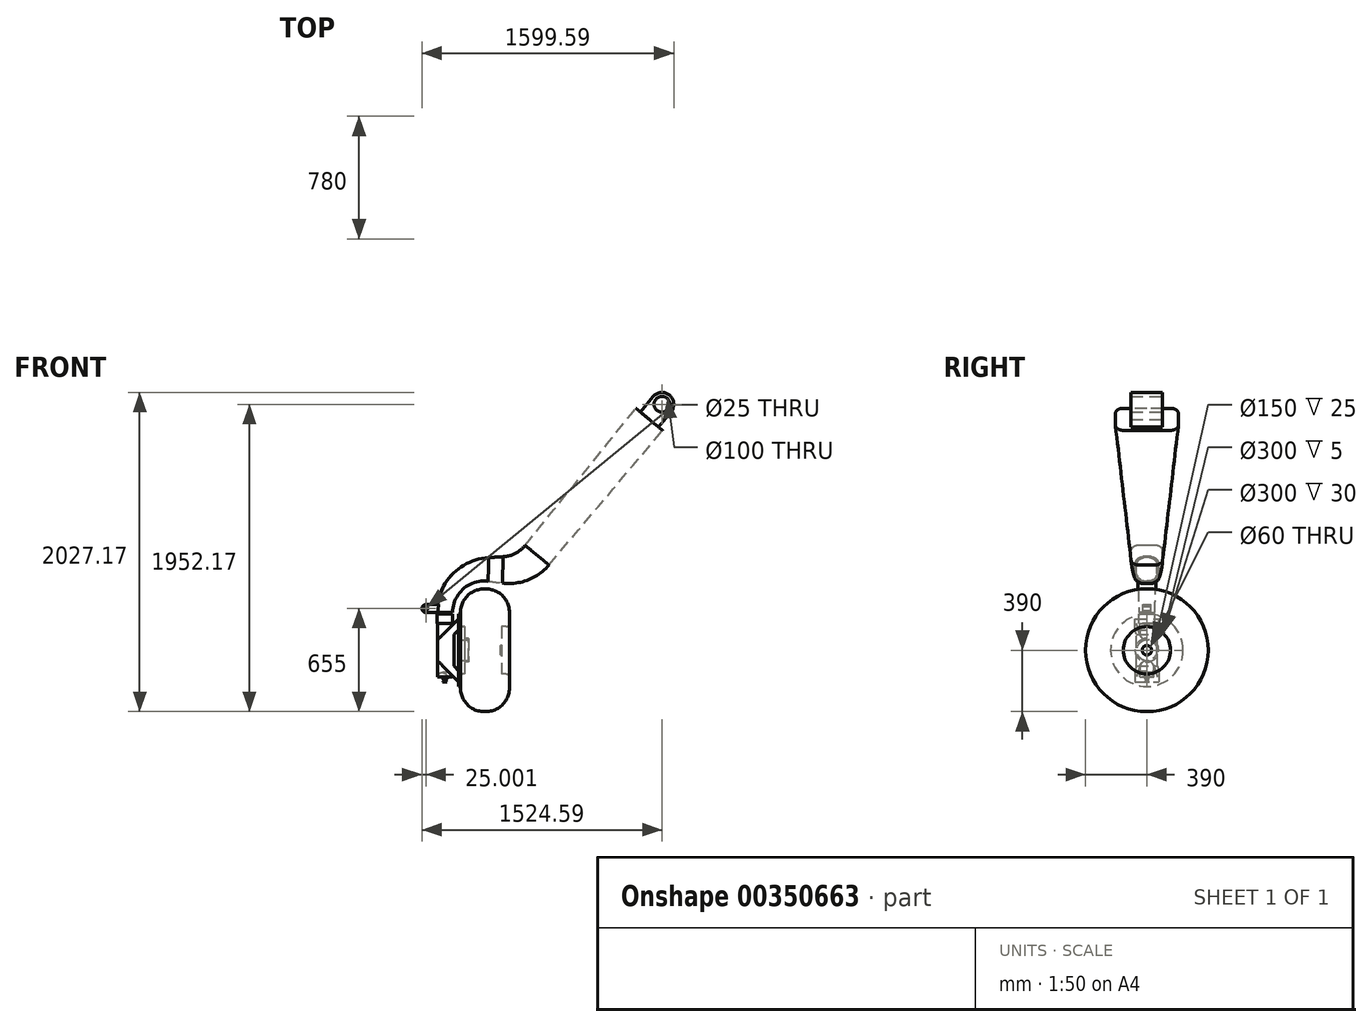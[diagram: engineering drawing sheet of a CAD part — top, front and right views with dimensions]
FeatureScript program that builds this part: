
annotation { "Feature Type Name" : "Feature", "Feature Type Description" : "" }
export const myFeature = defineFeature(function(context is Context, id is Id, definition is map)
    precondition{}
    {
        {
            var Q0;
            Q0=qCreatedBy(makeId("Front.planeOp"),FACE);
            var sketch = newSketch(context, id + "F0", { "sketchPlane" : qUnion([Q0])});
            skLineSegment(sketch, "E0.top", {"start": v(-5, 390) * mm, "end": v(5, 390) * mm});
            skLineSegment(sketch, "E0.left", {"start": v(-155, 170) * mm, "end": v(-155, 240) * mm});
            skLineSegment(sketch, "E0.right", {"start": v(155, 170) * mm, "end": v(155, 240) * mm});
            skPoint(sketch, "E1.visualSharp", {"position": v(-155, 390) * mm});
            skArc(sketch, "E1.filletArc", {"start": v(-5, 390) * mm, "mid": v(-111.07, 346.07) * mm, "end": v(-155, 240) * mm});
            skPoint(sketch, "E2.visualSharp", {"position": v(155, 390) * mm});
            skArc(sketch, "E2.filletArc", {"start": v(155, 240) * mm, "mid": v(111.07, 346.07) * mm, "end": v(5, 390) * mm});
            skLineSegment(sketch, "E3", {"start": v(-130, 75) * mm, "end": v(-105, 75) * mm});
            skLineSegment(sketch, "E4", {"start": v(-105, 75) * mm, "end": v(-105, 30) * mm});
            skLineSegment(sketch, "E5", {"start": v(-105, 30) * mm, "end": v(105, 30) * mm});
            skLineSegment(sketch, "E6", {"start": v(105, 30) * mm, "end": v(105, 150) * mm});
            skLineSegment(sketch, "E7", {"start": v(105, 150) * mm, "end": v(135, 150) * mm});
            skPoint(sketch, "E8.orphan", {"position": v(-155, 0) * mm});
            skPoint(sketch, "E9.visualSharp", {"position": v(155, 150) * mm});
            skArc(sketch, "E9.filletArc", {"start": v(135, 150) * mm, "mid": v(149.14, 155.86) * mm, "end": v(155, 170) * mm});
            skLineSegment(sketch, "E10", {"start": v(-280.75, 0) * mm, "end": v(393.95, 0) * mm});
            skLineSegment(sketch, "E11", {"start": v(-135, 150) * mm, "end": v(-130, 150) * mm});
            skLineSegment(sketch, "E12", {"start": v(-130, 150) * mm, "end": v(-130, 75) * mm});
            skPoint(sketch, "E13.visualSharp", {"position": v(-155, 150) * mm});
            skArc(sketch, "E13.filletArc", {"start": v(-155, 170) * mm, "mid": v(-149.14, 155.86) * mm, "end": v(-135, 150) * mm});
            skSolve(sketch);
        }
        {
            var Q0;
            Q0=qCreatedBy(makeId("Front.planeOp"),FACE);
            var sketch = newSketch(context, id + "F1", { "sketchPlane" : qUnion([Q0])});
            skLineSegment(sketch, "E14", {"start": v(-167, 230.07) * mm, "end": v(-157, 230.07) * mm});
            skLineSegment(sketch, "E15", {"start": v(-157, 230.07) * mm, "end": v(-157, 65) * mm});
            skLineSegment(sketch, "E16", {"start": v(-157, 65) * mm, "end": v(-105, 65) * mm});
            skLineSegment(sketch, "E17", {"start": v(-105, 65) * mm, "end": v(-105, 30) * mm});
            skLineSegment(sketch, "E18", {"start": v(-105, 30) * mm, "end": v(100, 30) * mm});
            skLineSegment(sketch, "E19", {"start": v(105, 25) * mm, "end": v(105, 0) * mm});
            skLineSegment(sketch, "E20", {"start": v(105, 0) * mm, "end": v(-167, 0) * mm});
            skLineSegment(sketch, "E21", {"start": v(-167, 0) * mm, "end": v(-167, 230.07) * mm});
            skPoint(sketch, "E22.visualSharp", {"position": v(105, 30) * mm});
            skArc(sketch, "E22.filletArc", {"start": v(105, 25) * mm, "mid": v(103.54, 28.54) * mm, "end": v(100, 30) * mm});
            skSolve(sketch);
        }
        {
            var Q0;
            Q0=qCreatedBy(makeId("Front.planeOp"),FACE);
            var sketch = newSketch(context, id + "F2", { "sketchPlane" : qUnion([Q0])});
            skLineSegment(sketch, "E23", {"start": v(-205, 0) * mm, "end": v(-205, 240) * mm});
            skLineSegment(sketch, "E24", {"start": v(-305, 0) * mm, "end": v(-305, 240) * mm});
            skArc(sketch, "E25", {"start": v(20.62, 438.35) * mm, "mid": v(-137.05, 390.2) * mm, "end": v(-205, 240) * mm});
            skLineSegment(sketch, "E26", {"start": v(-205, 240) * mm, "end": v(-305, 240) * mm, "construction": true});
            skLineSegment(sketch, "E27", {"start": v(20.62, 438.35) * mm, "end": v(22.33, 588.34) * mm, "construction": true});
            skArc(sketch, "E28", {"start": v(22.33, 588.34) * mm, "mid": v(-210.33, 479) * mm, "end": v(-305, 240) * mm});
            skLineSegment(sketch, "E29", {"start": v(22.33, 588.34) * mm, "end": v(89.49, 592.52) * mm});
            skArc(sketch, "E30", {"start": v(401.06, 544.79) * mm, "mid": v(264.57, 448.23) * mm, "end": v(98.57, 428.28) * mm});
            skArc(sketch, "E31", {"start": v(89.49, 592.52) * mm, "mid": v(177.07, 616.48) * mm, "end": v(247.85, 673.34) * mm});
            skLineSegment(sketch, "E32", {"start": v(247.85, 673.34) * mm, "end": v(401.06, 544.79) * mm, "construction": true});
            skLineSegment(sketch, "E33", {"start": v(324.45, 609.07) * mm, "end": v(1043.85, 1466.41) * mm});
            skLineSegment(sketch, "E34", {"start": v(401.06, 544.79) * mm, "end": v(1128.12, 1395.7) * mm});
            skLineSegment(sketch, "E35", {"start": v(247.85, 673.34) * mm, "end": v(959.59, 1537.12) * mm});
            skLineSegment(sketch, "E36", {"start": v(959.59, 1537.12) * mm, "end": v(1128.12, 1395.7) * mm, "construction": true});
            skArc(sketch, "E37", {"start": v(21.47, 513.35) * mm, "mid": v(-173.83, 434.4) * mm, "end": v(-255, 240) * mm});
            skLineSegment(sketch, "E38", {"start": v(21.47, 513.35) * mm, "end": v(113.82, 512.3) * mm});
            skArc(sketch, "E39", {"start": v(113.82, 512.3) * mm, "mid": v(230, 537.02) * mm, "end": v(324.45, 609.07) * mm});
            skLineSegment(sketch, "E40", {"start": v(20.62, 438.35) * mm, "end": v(98.57, 428.28) * mm});
            skSolve(sketch);
        }
        {
            var Q0;
            Q0=qCreatedBy(makeId("Front.planeOp"),FACE);
            var sketch = newSketch(context, id + "F3", { "sketchPlane" : qUnion([Q0])});
            skLineSegment(sketch, "E41.0", {"start": v(-205, 0) * mm, "end": v(-205, 240) * mm, "construction": true});
            skLineSegment(sketch, "E42.0", {"start": v(-305, 0) * mm, "end": v(-305, 240) * mm, "construction": true});
            skLineSegment(sketch, "E43", {"start": v(-305, 240) * mm, "end": v(-205, 240) * mm, "construction": true});
            skLineSegment(sketch, "E44", {"start": v(-255, 230) * mm, "end": v(-255, 0) * mm, "construction": true});
            skPoint(sketch, "E44.startSnap0", {"position": v(-255, 240) * mm});
            skLineSegment(sketch, "E45", {"start": v(-210, 0) * mm, "end": v(-210, 170) * mm});
            skLineSegment(sketch, "E46", {"start": v(-210, 170) * mm, "end": v(-205, 170) * mm});
            skLineSegment(sketch, "E47", {"start": v(-255, 230) * mm, "end": v(-205, 230) * mm, "construction": true});
            skLineSegment(sketch, "E48", {"start": v(-205, 230) * mm, "end": v(-205, 170) * mm});
            skLineSegment(sketch, "E49", {"start": v(-225, 230) * mm, "end": v(-225, 0.12) * mm});
            skPoint(sketch, "E49.endSnap0", {"position": v(-217.5, 0.12) * mm});
            skLineSegment(sketch, "E50", {"start": v(-225, 230) * mm, "end": v(-205, 230) * mm});
            skLineSegment(sketch, "E51", {"start": v(-210, 0) * mm, "end": v(-210, -170) * mm});
            skLineSegment(sketch, "E52", {"start": v(-225, -200) * mm, "end": v(-240, -200) * mm});
            skLineSegment(sketch, "E53", {"start": v(-225, -100) * mm, "end": v(-225, 0.12) * mm});
            skLineSegment(sketch, "E54", {"start": v(-225, -200) * mm, "end": v(-255, -200) * mm});
            skLineSegment(sketch, "E55", {"start": v(-255, -200) * mm, "end": v(-255, -100) * mm});
            skLineSegment(sketch, "E56", {"start": v(-255, -100) * mm, "end": v(-225, -100) * mm});
            skPoint(sketch, "E57.visualSharp", {"position": v(-210, -200) * mm});
            skArc(sketch, "E57.filletArc", {"start": v(-240, -200) * mm, "mid": v(-218.79, -191.21) * mm, "end": v(-210, -170) * mm});
            skSolve(sketch);
        }
        {
            var Q0;
            Q0=qCreatedBy(makeId("Front.planeOp"),FACE);
            var sketch = newSketch(context, id + "F4", { "sketchPlane" : qUnion([Q0])});
            skPoint(sketch, "E58.0", {"position": v(-167, 115.04) * mm});
            skLineSegment(sketch, "E59.0", {"start": v(-167, 115.04) * mm, "end": v(-167, 200) * mm});
            skPoint(sketch, "E60.orphan", {"position": v(-255, 230) * mm});
            skPoint(sketch, "E61.orphan", {"position": v(-167, 230.07) * mm});
            skLineSegment(sketch, "E62", {"start": v(-167, 200) * mm, "end": v(-367, 0) * mm});
            skLineSegment(sketch, "E63", {"start": v(-367, 0) * mm, "end": v(-197, 0) * mm});
            skLineSegment(sketch, "E64", {"start": v(-167, 130) * mm, "end": v(-197, 100) * mm});
            skLineSegment(sketch, "E65", {"start": v(-197, 100) * mm, "end": v(-197, 0) * mm});
            skPoint(sketch, "E66.orphan", {"position": v(-167, 0) * mm});
            skSolve(sketch);
        }
        {
            var Q0;
            Q0=qCreatedBy(makeId("Top.planeOp"),FACE);
            var sketch = newSketch(context, id + "F5", { "sketchPlane" : qUnion([Q0])});
            skPoint(sketch, "E67.0", {"position": v(-210, 0) * mm});
            skPoint(sketch, "E68.0", {"position": v(-255, 0) * mm});
            skLineSegment(sketch, "E69", {"start": v(-167, -75) * mm, "end": v(-367, -75) * mm});
            skLineSegment(sketch, "E70", {"start": v(-367, -75) * mm, "end": v(-367, 75) * mm});
            skLineSegment(sketch, "E71", {"start": v(-367, 75) * mm, "end": v(-167, 75) * mm});
            skLineSegment(sketch, "E72", {"start": v(-167, -75) * mm, "end": v(-167, 75) * mm, "construction": true});
            skCircle(sketch, "E73", {"center": v(-255, 0) * mm, "radius": 45 * mm, "construction": true});
            skArc(sketch, "E74.0", {"start": v(-268.31, 45.07) * mm, "mid": v(-302, 0) * mm, "end": v(-268.31, -45.07) * mm});
            skLineSegment(sketch, "E75", {"start": v(-268.31, -45.07) * mm, "end": v(-167, -75) * mm});
            skLineSegment(sketch, "E76", {"start": v(-268.31, 45.07) * mm, "end": v(-167, 75) * mm});
            skSolve(sketch);
        }
        {
            var Q0;
            Q0=sQuery(id+"F2.wireOp",EDGE,"E37");
            var Q1;
            Q1=sQuery(id+"F3.wireOp",VERTEX,"E44.startSnap0");
            cPlane(context, id + "F6", {"entities" : qUnion([Q0, Q1]), "cplaneType" : CPlaneType.CURVE_POINT, "offset" : 25 * mm, "width" : 150 * mm, "height" : 150 * mm});
        }
        {
            var Q0;
            Q0=sQuery(id+"F2.wireOp",EDGE,"E37");
            var Q1;
            Q1=sQuery(id+"F2.wireOp",VERTEX,"E37.start");
            cPlane(context, id + "F7", {"entities" : qUnion([Q0, Q1]), "cplaneType" : CPlaneType.CURVE_POINT, "offset" : 25 * mm, "width" : 150 * mm, "height" : 150 * mm});
        }
        {
            var Q0;
            Q0=qCreatedBy(id+"F6.planeOp",FACE);
            var sketch = newSketch(context, id + "F8", { "sketchPlane" : qUnion([Q0])});
            skPoint(sketch, "E77.0", {"position": v(-205, 0) * mm});
            skPoint(sketch, "E78.0", {"position": v(-255, 0) * mm});
            skCircle(sketch, "E79", {"center": v(-255, 0) * mm, "radius": 50 * mm});
            skSolve(sketch);
        }
        {
            var Q0;
            Q0=qCreatedBy(makeId("Front.planeOp"),FACE);
            var sketch = newSketch(context, id + "F9", { "sketchPlane" : qUnion([Q0])});
            skPoint(sketch, "E80.0", {"position": v(-205, 240) * mm});
            skPoint(sketch, "E81.0", {"position": v(20.62, 438.35) * mm});
            skArc(sketch, "E82", {"start": v(20.62, 438.35) * mm, "mid": v(-137.05, 390.2) * mm, "end": v(-205, 240) * mm});
            skPoint(sketch, "E83.0", {"position": v(-305, 240) * mm});
            skPoint(sketch, "E84.0", {"position": v(22.33, 588.34) * mm});
            skArc(sketch, "E85", {"start": v(22.33, 588.34) * mm, "mid": v(-210.33, 479) * mm, "end": v(-305, 240) * mm});
            skSolve(sketch);
        }
        {
            var Q0;
            Q0=qCreatedBy(id+"F7.planeOp",FACE);
            var sketch = newSketch(context, id + "F10", { "sketchPlane" : qUnion([Q0])});
            skPoint(sketch, "E86.0", {"position": v(0, 513.56) * mm});
            skLineSegment(sketch, "E87.bottom", {"start": v(-15, 438.56) * mm, "end": v(15, 438.56) * mm});
            skLineSegment(sketch, "E87.top", {"start": v(-15, 588.56) * mm, "end": v(15, 588.56) * mm});
            skLineSegment(sketch, "E87.left", {"start": v(-65, 488.56) * mm, "end": v(-65, 538.56) * mm});
            skLineSegment(sketch, "E87.right", {"start": v(65, 488.56) * mm, "end": v(65, 538.56) * mm});
            skPoint(sketch, "E88.0", {"position": v(0, 438.56) * mm});
            skPoint(sketch, "E89.visualSharp", {"position": v(65, 588.56) * mm});
            skArc(sketch, "E89.filletArc", {"start": v(65, 538.56) * mm, "mid": v(50.36, 573.91) * mm, "end": v(15, 588.56) * mm});
            skPoint(sketch, "E90.visualSharp", {"position": v(-65, 588.56) * mm});
            skArc(sketch, "E90.filletArc", {"start": v(-15, 588.56) * mm, "mid": v(-50.36, 573.91) * mm, "end": v(-65, 538.56) * mm});
            skPoint(sketch, "E91.visualSharp", {"position": v(-65, 438.56) * mm});
            skArc(sketch, "E91.filletArc", {"start": v(-65, 488.56) * mm, "mid": v(-50.36, 453.2) * mm, "end": v(-15, 438.56) * mm});
            skPoint(sketch, "E92.visualSharp", {"position": v(65, 438.56) * mm});
            skArc(sketch, "E92.filletArc", {"start": v(15, 438.56) * mm, "mid": v(50.36, 453.2) * mm, "end": v(65, 488.56) * mm});
            skSolve(sketch);
        }
        {
            var Q0;
            Q0=qCreatedBy(makeId("Front.planeOp"),FACE);
            var sketch = newSketch(context, id + "F11", { "sketchPlane" : qUnion([Q0])});
            skPoint(sketch, "E93.0", {"position": v(20.62, 438.35) * mm});
            skPoint(sketch, "E94.0", {"position": v(22.33, 588.34) * mm});
            skLineSegment(sketch, "E95", {"start": v(20.62, 438.35) * mm, "end": v(111.11, 426.66) * mm});
            skLineSegment(sketch, "E96", {"start": v(22.33, 588.34) * mm, "end": v(116.4, 594.2) * mm});
            skLineSegment(sketch, "E97", {"start": v(116.4, 594.2) * mm, "end": v(111.11, 426.66) * mm});
            skLineSegment(sketch, "E98", {"start": v(113.76, 510.43) * mm, "end": v(21.47, 513.35) * mm, "construction": true});
            skSolve(sketch);
        }
        {
            var Q0;
            Q0=sQuery(id+"F11.wireOp",EDGE,"E98");
            var Q1;
            Q1=sQuery(id+"F11.wireOp",VERTEX,"E98.start");
            cPlane(context, id + "F12", {"entities" : qUnion([Q0, Q1]), "cplaneType" : CPlaneType.CURVE_POINT, "offset" : 25 * mm, "width" : 150 * mm, "height" : 150 * mm});
        }
        {
            var Q0;
            Q0=qCreatedBy(id+"F12.planeOp",FACE);
            var sketch = newSketch(context, id + "F13", { "sketchPlane" : qUnion([Q0])});
            skPoint(sketch, "E99.0", {"position": v(0, 513.77) * mm});
            skLineSegment(sketch, "E100.bottom", {"start": v(-25, 429.96) * mm, "end": v(25, 429.96) * mm});
            skLineSegment(sketch, "E100.top", {"start": v(-25, 597.58) * mm, "end": v(25, 597.58) * mm});
            skLineSegment(sketch, "E100.left", {"start": v(-75, 479.96) * mm, "end": v(-75, 547.58) * mm});
            skLineSegment(sketch, "E100.right", {"start": v(75, 479.96) * mm, "end": v(75, 547.58) * mm});
            skPoint(sketch, "E101.0", {"position": v(0, 597.58) * mm});
            skPoint(sketch, "E102.0", {"position": v(0, 429.96) * mm});
            skPoint(sketch, "E103.visualSharp", {"position": v(75, 429.96) * mm});
            skArc(sketch, "E103.filletArc", {"start": v(25, 429.96) * mm, "mid": v(60.36, 444.6) * mm, "end": v(75, 479.96) * mm});
            skPoint(sketch, "E104.visualSharp", {"position": v(75, 597.58) * mm});
            skArc(sketch, "E104.filletArc", {"start": v(75, 547.58) * mm, "mid": v(60.36, 582.93) * mm, "end": v(25, 597.58) * mm});
            skPoint(sketch, "E105.visualSharp", {"position": v(-75, 597.58) * mm});
            skArc(sketch, "E105.filletArc", {"start": v(-25, 597.58) * mm, "mid": v(-60.36, 582.93) * mm, "end": v(-75, 547.58) * mm});
            skPoint(sketch, "E106.visualSharp", {"position": v(-75, 429.96) * mm});
            skArc(sketch, "E106.filletArc", {"start": v(-75, 479.96) * mm, "mid": v(-60.36, 444.6) * mm, "end": v(-25, 429.96) * mm});
            skSolve(sketch);
        }
        {
            var Q0;
            Q0=qCreatedBy(makeId("Front.planeOp"),FACE);
            var sketch = newSketch(context, id + "F14", { "sketchPlane" : qUnion([Q0])});
            skPoint(sketch, "E107.0", {"position": v(111.11, 426.66) * mm});
            skPoint(sketch, "E108.0", {"position": v(116.4, 594.2) * mm});
            skArc(sketch, "E109", {"start": v(111.11, 426.66) * mm, "mid": v(273.33, 446.39) * mm, "end": v(406.34, 541.32) * mm});
            skArc(sketch, "E110", {"start": v(116.4, 594.2) * mm, "mid": v(193.48, 615.48) * mm, "end": v(255.46, 666) * mm});
            skLineSegment(sketch, "E111", {"start": v(406.34, 541.32) * mm, "end": v(255.46, 666) * mm});
            skLineSegment(sketch, "E112", {"start": v(330.9, 603.66) * mm, "end": v(1043.85, 1466.41) * mm, "construction": true});
            skLineSegment(sketch, "E113", {"start": v(406.34, 541.32) * mm, "end": v(1128.12, 1395.7) * mm, "construction": true});
            skLineSegment(sketch, "E114", {"start": v(255.46, 666) * mm, "end": v(959.59, 1537.12) * mm, "construction": true});
            skPoint(sketch, "E115.0", {"position": v(113.76, 510.43) * mm});
            skArc(sketch, "E116", {"start": v(113.76, 510.43) * mm, "mid": v(233.6, 530.78) * mm, "end": v(330.9, 603.66) * mm, "construction": true});
            skSolve(sketch);
        }
        {
            var Q0;
            Q0=sQuery(id+"F14.wireOp",EDGE,"E111");
            cPoint(context, id + "F15", {"entities" : qUnion([Q0]), "parameter" : 0.5});
        }
        {
            var Q0;
            Q0=sQuery(id+"F14.wireOp",EDGE,"E116");
            var Q1;
            Q1=qCreatedBy(id+"F15",VERTEX);
            cPlane(context, id + "F16", {"entities" : qUnion([Q0, Q1]), "cplaneType" : CPlaneType.CURVE_POINT, "offset" : 25 * mm, "width" : 150 * mm, "height" : 150 * mm});
        }
        {
            var Q0;
            Q0=qCreatedBy(id+"F16.planeOp",FACE);
            var sketch = newSketch(context, id + "F17", { "sketchPlane" : qUnion([Q0])});
            skPoint(sketch, "E117.0", {"position": v(-129.46, 0) * mm});
            skPoint(sketch, "E118.0", {"position": v(-31.6, 0) * mm});
            skLineSegment(sketch, "E119.bottom", {"start": v(-81.6, 100) * mm, "end": v(-177.32, 100) * mm});
            skLineSegment(sketch, "E119.top", {"start": v(-81.6, -100) * mm, "end": v(-177.32, -100) * mm});
            skLineSegment(sketch, "E119.left", {"start": v(-31.6, 50) * mm, "end": v(-31.6, -50) * mm});
            skLineSegment(sketch, "E119.right", {"start": v(-227.32, 50) * mm, "end": v(-227.32, -50) * mm});
            skPoint(sketch, "E120.visualSharp", {"position": v(-31.6, -100) * mm});
            skArc(sketch, "E120.filletArc", {"start": v(-81.6, -100) * mm, "mid": v(-46.25, -85.36) * mm, "end": v(-31.6, -50) * mm});
            skPoint(sketch, "E121.visualSharp", {"position": v(-227.32, -100) * mm});
            skArc(sketch, "E121.filletArc", {"start": v(-227.32, -50) * mm, "mid": v(-212.68, -85.36) * mm, "end": v(-177.32, -100) * mm});
            skPoint(sketch, "E122.visualSharp", {"position": v(-227.32, 100) * mm});
            skArc(sketch, "E122.filletArc", {"start": v(-177.32, 100) * mm, "mid": v(-212.68, 85.36) * mm, "end": v(-227.32, 50) * mm});
            skPoint(sketch, "E123.visualSharp", {"position": v(-31.6, 100) * mm});
            skArc(sketch, "E123.filletArc", {"start": v(-31.6, 50) * mm, "mid": v(-46.25, 85.36) * mm, "end": v(-81.6, 100) * mm});
            skSolve(sketch);
        }
        {
            var Q0;
            Q0=sQuery(id+"F14.wireOp",EDGE,"E112");
            var Q1;
            Q1=sQuery(id+"F14.wireOp",VERTEX,"E112.end");
            cPlane(context, id + "F18", {"entities" : qUnion([Q0, Q1]), "cplaneType" : CPlaneType.CURVE_POINT, "offset" : 25 * mm, "width" : 150 * mm, "height" : 150 * mm});
        }
        {
            var Q0;
            Q0=qCreatedBy(id+"F18.planeOp",FACE);
            var sketch = newSketch(context, id + "F19", { "sketchPlane" : qUnion([Q0])});
            skPoint(sketch, "E124.0", {"position": v(-129.46, 0) * mm});
            skPoint(sketch, "E125.0", {"position": v(-19.47, 0) * mm});
            skLineSegment(sketch, "E126.bottom", {"start": v(-69.47, 200) * mm, "end": v(-189.46, 200) * mm});
            skLineSegment(sketch, "E126.top", {"start": v(-69.47, -200) * mm, "end": v(-189.46, -200) * mm});
            skLineSegment(sketch, "E126.left", {"start": v(-19.47, 150) * mm, "end": v(-19.47, -150) * mm});
            skLineSegment(sketch, "E126.right", {"start": v(-239.46, 150) * mm, "end": v(-239.46, -150) * mm});
            skPoint(sketch, "E127.visualSharp", {"position": v(-239.46, -200) * mm});
            skArc(sketch, "E127.filletArc", {"start": v(-239.46, -150) * mm, "mid": v(-224.81, -185.36) * mm, "end": v(-189.46, -200) * mm});
            skPoint(sketch, "E128.visualSharp", {"position": v(-239.46, 200) * mm});
            skArc(sketch, "E128.filletArc", {"start": v(-189.46, 200) * mm, "mid": v(-224.81, 185.36) * mm, "end": v(-239.46, 150) * mm});
            skPoint(sketch, "E129.visualSharp", {"position": v(-19.47, 200) * mm});
            skArc(sketch, "E129.filletArc", {"start": v(-19.47, 150) * mm, "mid": v(-34.11, 185.36) * mm, "end": v(-69.47, 200) * mm});
            skPoint(sketch, "E130.visualSharp", {"position": v(-19.47, -200) * mm});
            skArc(sketch, "E130.filletArc", {"start": v(-69.47, -200) * mm, "mid": v(-34.11, -185.36) * mm, "end": v(-19.47, -150) * mm});
            skSolve(sketch);
        }
        {
            var Q0;
            Q0=qCreatedBy(makeId("Front.planeOp"),FACE);
            var sketch = newSketch(context, id + "F20", { "sketchPlane" : qUnion([Q0])});
            skPoint(sketch, "E131.0", {"position": v(406.34, 541.32) * mm});
            skPoint(sketch, "E132.0", {"position": v(1128.65, 1396.34) * mm});
            skPoint(sketch, "E133.0", {"position": v(255.46, 666) * mm});
            skPoint(sketch, "E134.0", {"position": v(959.06, 1536.48) * mm});
            skLineSegment(sketch, "E135", {"start": v(406.34, 541.32) * mm, "end": v(1128.65, 1396.34) * mm});
            skLineSegment(sketch, "E136", {"start": v(255.46, 666) * mm, "end": v(959.06, 1536.48) * mm});
            skSolve(sketch);
        }
        {
            var Q0;
            Q0=qCreatedBy(makeId("Front.planeOp"),FACE);
            var sketch = newSketch(context, id + "F21", { "sketchPlane" : qUnion([Q0])});
            skPoint(sketch, "E137.0", {"position": v(-255, 240) * mm});
            skPoint(sketch, "E138.0", {"position": v(-225, -100) * mm});
            skLineSegment(sketch, "E139.bottom", {"start": v(-255, 240) * mm, "end": v(-225, 240) * mm});
            skLineSegment(sketch, "E139.top", {"start": v(-255, -100) * mm, "end": v(-225, -100) * mm});
            skLineSegment(sketch, "E139.left", {"start": v(-255, 240) * mm, "end": v(-255, -100) * mm});
            skLineSegment(sketch, "E139.right", {"start": v(-225, 240) * mm, "end": v(-225, -100) * mm});
            skSolve(sketch);
        }
        {
            var Q0;
            Q0=qCreatedBy(makeId("Front.planeOp"),FACE);
            var sketch = newSketch(context, id + "F22", { "sketchPlane" : qUnion([Q0])});
            skPoint(sketch, "E140.0", {"position": v(-255, 240) * mm});
            skArc(sketch, "E141", {"start": v(-250.39, 290) * mm, "mid": v(-253.84, 265.1) * mm, "end": v(-255, 240) * mm});
            skLineSegment(sketch, "E142", {"start": v(-255, 240) * mm, "end": v(-375.39, 240) * mm});
            skLineSegment(sketch, "E143", {"start": v(-400.39, 265) * mm, "end": v(-400.39, 265) * mm});
            skLineSegment(sketch, "E144", {"start": v(-375.39, 290) * mm, "end": v(-250.39, 290) * mm});
            skPoint(sketch, "E145.visualSharp", {"position": v(-400.39, 290) * mm});
            skArc(sketch, "E145.filletArc", {"start": v(-375.39, 290) * mm, "mid": v(-393.07, 282.68) * mm, "end": v(-400.39, 265) * mm});
            skPoint(sketch, "E146.visualSharp", {"position": v(-400.39, 240) * mm});
            skArc(sketch, "E146.filletArc", {"start": v(-400.39, 265) * mm, "mid": v(-393.07, 247.32) * mm, "end": v(-375.39, 240) * mm});
            skCircle(sketch, "E147", {"center": v(-375.39, 265) * mm, "radius": 12.5 * mm});
            skSolve(sketch);
        }
        {
            var Q0;
            Q0=qCreatedBy(makeId("Front.planeOp"),FACE);
            var sketch = newSketch(context, id + "F23", { "sketchPlane" : qUnion([Q0])});
            skLineSegment(sketch, "E148.0", {"start": v(959.59, 1537.12) * mm, "end": v(1128.12, 1395.7) * mm});
            skLineSegment(sketch, "E149", {"start": v(986.4, 1514.62) * mm, "end": v(1066.75, 1610.38) * mm});
            skLineSegment(sketch, "E150", {"start": v(1172.41, 1619.62) * mm, "end": v(1172.41, 1619.62) * mm});
            skLineSegment(sketch, "E151", {"start": v(1181.66, 1513.96) * mm, "end": v(1101.3, 1418.2) * mm});
            skLineSegment(sketch, "E152", {"start": v(1172.41, 1619.62) * mm, "end": v(1043.85, 1466.41) * mm, "construction": true});
            skPoint(sketch, "E153.visualSharp", {"position": v(1114.96, 1667.83) * mm});
            skArc(sketch, "E153.filletArc", {"start": v(1172.41, 1619.62) * mm, "mid": v(1117.67, 1636.88) * mm, "end": v(1066.75, 1610.38) * mm});
            skPoint(sketch, "E154.visualSharp", {"position": v(1229.87, 1571.41) * mm});
            skArc(sketch, "E154.filletArc", {"start": v(1181.66, 1513.96) * mm, "mid": v(1198.92, 1568.7) * mm, "end": v(1172.41, 1619.62) * mm});
            skCircle(sketch, "E155", {"center": v(1124.2, 1562.17) * mm, "radius": 50 * mm});
            skSolve(sketch);
        }
        {
            var Q0;
            Q0=makeQuery(id+"F0.imprint","IMPRINT",FACE,{"disambiguationData":[TD([[makeQuery(id+"F0.imprint","IMPRINT",EDGE,{"derivedFrom":sQuery(id+"F0.wireOp",EDGE,"E0.top")}),-1.0]])]});
            var Q1;
            Q1=sQuery(id+"F0.wireOp",EDGE,"E10");
            revolve(context, id + "F24", {"entities" : qUnion([Q0]), "axis" : qUnion([Q1]), "revolveType" : RevolveType.FULL});
        }
        {
            var Q0;
            {var subQ1=sQuery(id+"F4.wireOp",EDGE,"E62");Q0=makeQuery(id+"F4.imprint","IMPRINT",FACE,{"disambiguationData":[TD([[makeQuery(id+"F4.imprint","IMPRINT",EDGE,{"derivedFrom":subQ1}),1.0]])]});}
            extrude(context, id + "F25", {"entities" : qUnion([Q0]), "endBound" : BoundingType.SYMMETRIC, "depth" : 150 * mm});
        }
        {
            var Q0;
            Q0=makeQuery(id+"F5.imprint","IMPRINT",FACE,{"disambiguationData":[TD([[makeQuery(id+"F5.imprint","IMPRINT",EDGE,{"derivedFrom":sQuery(id+"F5.wireOp",EDGE,"E69")}),-1.0]])]});
            extrude(context, id + "F26", {"entities" : qUnion([Q0]), "operationType" : NewBodyOperationType.REMOVE, "endBound" : BoundingType.THROUGH_ALL, "depth" : 25 * mm});
        }
        {
            var Q0;
            Q0=makeQuery(id+"F25.opExtrude","SWEPT_BODY",BODY,{"disambiguationData":[OSD([sQuery(id+"F4.wireOp",EDGE,"E59.0"),sQuery(id+"F4.wireOp",EDGE,"E62"),sQuery(id+"F4.wireOp",EDGE,"E63"),sQuery(id+"F4.wireOp",EDGE,"E64"),sQuery(id+"F4.wireOp",EDGE,"E65")])]});
            var Q1;
            Q1=makeQuery(id+"F25.opExtrude","SWEPT_FACE",FACE,{"disambiguationData":[OSD([sQuery(id+"F4.wireOp",EDGE,"E63")])]});
            mirror(context, id + "F27", {"operationType" : NewBodyOperationType.ADD, "entities" : qUnion([Q0]), "mirrorPlane" : qUnion([Q1])});
        }
        {
            var Q0;
            Q0=makeQuery(id+"F3.imprint","IMPRINT",FACE,{"disambiguationData":[TD([[makeQuery(id+"F3.imprint","IMPRINT",EDGE,{"derivedFrom":sQuery(id+"F3.wireOp",EDGE,"E45")}),1.0]])]});
            var Q1;
            Q1=sQuery(id+"F3.wireOp",EDGE,"E44");
            revolve(context, id + "F28", {"operationType" : NewBodyOperationType.ADD, "entities" : qUnion([Q0]), "axis" : qUnion([Q1]), "revolveType" : RevolveType.FULL});
        }
        {
            var Q0;
            Q0=makeQuery(id+"F1.imprint","IMPRINT",FACE,{"disambiguationData":[TD([[makeQuery(id+"F1.imprint","IMPRINT",EDGE,{"derivedFrom":sQuery(id+"F1.wireOp",EDGE,"E14")}),-1.0]])]});
            var Q1;
            Q1=sQuery(id+"F1.wireOp",EDGE,"E20");
            revolve(context, id + "F29", {"operationType" : NewBodyOperationType.ADD, "entities" : qUnion([Q0]), "axis" : qUnion([Q1]), "revolveType" : RevolveType.FULL});
        }
        {
            var Q0;
            Q0=makeQuery(id+"F8.imprint","IMPRINT",FACE,{"disambiguationData":[TD([[makeQuery(id+"F8.imprint","IMPRINT",EDGE,{"derivedFrom":sQuery(id+"F8.wireOp",EDGE,"E79")}),1.0]])]});
            var Q1;
            Q1=makeQuery(id+"F10.imprint","IMPRINT",FACE,{"disambiguationData":[TD([[makeQuery(id+"F10.imprint","IMPRINT",EDGE,{"derivedFrom":sQuery(id+"F10.wireOp",EDGE,"E87.bottom")}),1.0]])]});
            var Q2;
            Q2=sQuery(id+"F9.wireOp",EDGE,"E85");
            var Q3;
            Q3=sQuery(id+"F9.wireOp",EDGE,"E82");
            loft(context, id + "F30", {"addGuides" : true, "sheetProfilesArray" : [{ "sheetProfileEntities" : qUnion([Q0]) }, { "sheetProfileEntities" : qUnion([Q1]) }], "guidesArray" : [{ "guideEntities" : qUnion([Q2]), "guideDerivativeType" : LoftGuideDerivativeType.DEFAULT, "guideDerivativeMagnitude" : 1 }, { "guideEntities" : qUnion([Q3]), "guideDerivativeType" : LoftGuideDerivativeType.DEFAULT, "guideDerivativeMagnitude" : 1 }]});
        }
        {
            var Q1;
            Q1=makeQuery(id+"F10.imprint","IMPRINT",FACE,{"disambiguationData":[TD([[makeQuery(id+"F10.imprint","IMPRINT",EDGE,{"derivedFrom":sQuery(id+"F10.wireOp",EDGE,"E87.bottom")}),1.0]])]});
            var Q2;
            Q2=makeQuery(id+"F13.imprint","IMPRINT",FACE,{"disambiguationData":[TD([[makeQuery(id+"F13.imprint","IMPRINT",EDGE,{"derivedFrom":sQuery(id+"F13.wireOp",EDGE,"E100.bottom")}),1.0]])]});
            var Q3;
            Q3=sQuery(id+"F11.wireOp",EDGE,"E96");
            var Q4;
            Q4=sQuery(id+"F11.wireOp",EDGE,"E95");
            loft(context, id + "F31", {"operationType" : NewBodyOperationType.ADD, "addGuides" : true, "sheetProfilesArray" : [{ "sheetProfileEntities" : qUnion([Q1]) }, { "sheetProfileEntities" : qUnion([Q2]) }], "guidesArray" : [{ "guideEntities" : qUnion([Q3]), "guideDerivativeType" : LoftGuideDerivativeType.DEFAULT, "guideDerivativeMagnitude" : 1 }, { "guideEntities" : qUnion([Q4]), "guideDerivativeType" : LoftGuideDerivativeType.DEFAULT, "guideDerivativeMagnitude" : 1 }]});
        }
        {
            var Q1;
            Q1=makeQuery(id+"F13.imprint","IMPRINT",FACE,{"disambiguationData":[TD([[makeQuery(id+"F13.imprint","IMPRINT",EDGE,{"derivedFrom":sQuery(id+"F13.wireOp",EDGE,"E100.bottom")}),1.0]])]});
            var Q2;
            Q2=makeQuery(id+"F17.imprint","IMPRINT",FACE,{"disambiguationData":[TD([[makeQuery(id+"F17.imprint","IMPRINT",EDGE,{"derivedFrom":sQuery(id+"F17.wireOp",EDGE,"E119.bottom")}),1.0]])]});
            var Q3;
            Q3=sQuery(id+"F14.wireOp",EDGE,"E109");
            var Q4;
            Q4=sQuery(id+"F14.wireOp",EDGE,"E110");
            loft(context, id + "F32", {"operationType" : NewBodyOperationType.ADD, "addGuides" : true, "sheetProfilesArray" : [{ "sheetProfileEntities" : qUnion([Q1]) }, { "sheetProfileEntities" : qUnion([Q2]) }], "guidesArray" : [{ "guideEntities" : qUnion([Q3]), "guideDerivativeType" : LoftGuideDerivativeType.DEFAULT, "guideDerivativeMagnitude" : 1 }, { "guideEntities" : qUnion([Q4]), "guideDerivativeType" : LoftGuideDerivativeType.DEFAULT, "guideDerivativeMagnitude" : 1 }]});
        }
        {
            var Q1;
            Q1=makeQuery(id+"F17.imprint","IMPRINT",FACE,{"disambiguationData":[TD([[makeQuery(id+"F17.imprint","IMPRINT",EDGE,{"derivedFrom":sQuery(id+"F17.wireOp",EDGE,"E119.bottom")}),1.0]])]});
            var Q2;
            Q2=makeQuery(id+"F19.imprint","IMPRINT",FACE,{"disambiguationData":[TD([[makeQuery(id+"F19.imprint","IMPRINT",EDGE,{"derivedFrom":sQuery(id+"F19.wireOp",EDGE,"E126.bottom")}),1.0]])]});
            var Q3;
            Q3=sQuery(id+"F20.wireOp",EDGE,"E136");
            var Q4;
            Q4=sQuery(id+"F20.wireOp",EDGE,"E135");
            loft(context, id + "F33", {"operationType" : NewBodyOperationType.ADD, "addGuides" : true, "sheetProfilesArray" : [{ "sheetProfileEntities" : qUnion([Q1]) }, { "sheetProfileEntities" : qUnion([Q2]) }], "guidesArray" : [{ "guideEntities" : qUnion([Q3]), "guideDerivativeType" : LoftGuideDerivativeType.DEFAULT, "guideDerivativeMagnitude" : 1 }, { "guideEntities" : qUnion([Q4]), "guideDerivativeType" : LoftGuideDerivativeType.DEFAULT, "guideDerivativeMagnitude" : 1 }]});
        }
        {
            var Q0;
            Q0=makeQuery(id+"F22.imprint","IMPRINT",FACE,{"disambiguationData":[TD([[makeQuery(id+"F22.imprint","IMPRINT",EDGE,{"derivedFrom":sQuery(id+"F22.wireOp",EDGE,"E141")}),-1.0]])]});
            extrude(context, id + "F34", {"entities" : qUnion([Q0]), "operationType" : NewBodyOperationType.ADD, "endBound" : BoundingType.SYMMETRIC, "depth" : 50 * mm});
        }
        {
            var Q0;
            {var subQ1=sQuery(id+"F23.wireOp",EDGE,"E149");Q0=makeQuery(id+"F23.imprint","IMPRINT",FACE,{"disambiguationData":[TD([[makeQuery(id+"F23.imprint","IMPRINT",EDGE,{"derivedFrom":subQ1}),-1.0]])]});}
            extrude(context, id + "F35", {"entities" : qUnion([Q0]), "operationType" : NewBodyOperationType.ADD, "endBound" : BoundingType.SYMMETRIC, "depth" : 200 * mm});
        }
        {
            var Q0;
            Q0=makeQuery(id+"F21.imprint","IMPRINT",FACE,{"disambiguationData":[TD([[makeQuery(id+"F21.imprint","IMPRINT",EDGE,{"derivedFrom":sQuery(id+"F21.wireOp",EDGE,"E139.bottom")}),-1.0]])]});
            var Q1;
            Q1=sQuery(id+"F21.wireOp",EDGE,"E139.left");
            revolve(context, id + "F36", {"operationType" : NewBodyOperationType.ADD, "entities" : qUnion([Q0]), "axis" : qUnion([Q1]), "revolveType" : RevolveType.FULL});
        }
    });
